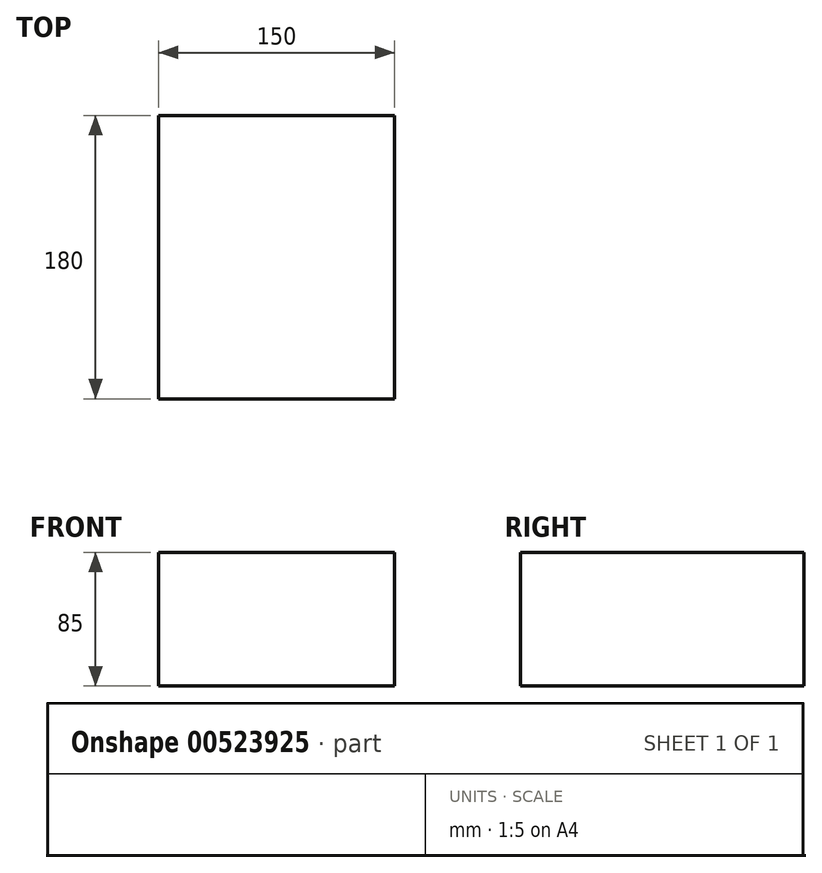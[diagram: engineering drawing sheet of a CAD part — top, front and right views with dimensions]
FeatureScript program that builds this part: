
annotation { "Feature Type Name" : "Feature", "Feature Type Description" : "" }
export const myFeature = defineFeature(function(context is Context, id is Id, definition is map)
    precondition{}
    {
        {
            var Q0;
            Q0=qCreatedBy(makeId("Front.planeOp"),FACE);
            var sketch = newSketch(context, id + "F0", { "sketchPlane" : qUnion([Q0])});
            skCircle(sketch, "E0", {"center": v(0, 0) * mm, "radius": 30 * mm});
            skSolve(sketch);
        }
        {
            var Q0;
            Q0=qSketchRegion(id+"F0",true);
            extrude(context, id + "F1", {"entities" : qUnion([Q0]), "depth" : 190 * mm});
        }
        {
            var Q0;
            Q0=makeQuery(id+"F1.opExtrude","CAP_FACE",FACE,{"disambiguationData":[OSD([sQuery(id+"F0.wireOp",EDGE,"E0")])],"isStart":true});
            var sketch = newSketch(context, id + "F2", { "sketchPlane" : qUnion([Q0])});
            skArc(sketch, "E1", {"start": v(0, 40) * mm, "mid": v(-40, 0) * mm, "end": v(0, -40) * mm});
            skLineSegment(sketch, "E2", {"start": v(0, 40) * mm, "end": v(50, 40) * mm});
            skLineSegment(sketch, "E3", {"start": v(50, 40) * mm, "end": v(50, -40) * mm});
            skLineSegment(sketch, "E4", {"start": v(50, -40) * mm, "end": v(0, -40) * mm});
            skSolve(sketch);
        }
        {
            var Q0;
            Q0=qSketchRegion(id+"F2",true);
            extrude(context, id + "F3", {"entities" : qUnion([Q0]), "operationType" : NewBodyOperationType.ADD, "oppositeDirection" : true, "depth" : 25 * mm});
        }
        {
            var Q0;
            Q0=makeQuery(id+"F3.opExtrude","CAP_FACE",FACE,{"disambiguationData":[OSD([sQuery(id+"F2.wireOp",EDGE,"E1"),sQuery(id+"F2.wireOp",EDGE,"E2"),sQuery(id+"F2.wireOp",EDGE,"E3"),sQuery(id+"F2.wireOp",EDGE,"E4")])],"isStart":false});
            var sketch = newSketch(context, id + "F4", { "sketchPlane" : qUnion([Q0])});
            skCircle(sketch, "E5", {"center": v(0, 0) * mm, "radius": 40 * mm});
            skSolve(sketch);
        }
        {
            var Q0;
            Q0=qSketchRegion(id+"F4",true);
            extrude(context, id + "F5", {"entities" : qUnion([Q0]), "operationType" : NewBodyOperationType.ADD, "depth" : 35 * mm});
        }
        {
            var Q0;
            Q0=qCreatedBy(makeId("Front.planeOp"),FACE);
            var sketch = newSketch(context, id + "F6", { "sketchPlane" : qUnion([Q0])});
            skLineSegment(sketch, "E6.bottom", {"start": v(0, 0) * mm, "end": v(170, 0) * mm});
            skLineSegment(sketch, "E6.top", {"start": v(0, 170) * mm, "end": v(170, 170) * mm});
            skLineSegment(sketch, "E6.left", {"start": v(0, 0) * mm, "end": v(0, 170) * mm});
            skLineSegment(sketch, "E6.right", {"start": v(170, 0) * mm, "end": v(170, 170) * mm});
            skCircle(sketch, "E7", {"center": v(6.35, 159.84) * mm, "radius": 2 * mm});
            skCircle(sketch, "E8", {"center": v(163.83, 136.98) * mm, "radius": 2 * mm});
            skCircle(sketch, "E9", {"center": v(163.83, 4.9) * mm, "radius": 2 * mm});
            skCircle(sketch, "E10", {"center": v(6.35, 4.9) * mm, "radius": 2 * mm});
            skSolve(sketch);
        }
        {
            var Q0;
            Q0=qSketchRegion(id+"F6",true);
            extrude(context, id + "F7", {"entities" : qUnion([Q0]), "depth" : 2 * mm});
        }
        {
            var Q0;
            Q0=makeQuery(id+"F7.opExtrude","SWEPT_BODY",BODY,{"disambiguationData":[OSD([sQuery(id+"F6.wireOp",EDGE,"E6.bottom"),sQuery(id+"F6.wireOp",EDGE,"E6.top"),sQuery(id+"F6.wireOp",EDGE,"E6.left"),sQuery(id+"F6.wireOp",EDGE,"E6.right"),sQuery(id+"F6.wireOp",EDGE,"E7"),sQuery(id+"F6.wireOp",EDGE,"E8"),sQuery(id+"F6.wireOp",EDGE,"E9"),sQuery(id+"F6.wireOp",EDGE,"E10")])]});
            deleteBodies(context, id + "F8", {"entities" : qUnion([Q0])});
        }
        {
            var Q0;
            Q0=qCreatedBy(makeId("Front.planeOp"),FACE);
            var sketch = newSketch(context, id + "F9", { "sketchPlane" : qUnion([Q0])});
            skLineSegment(sketch, "E11.bottom", {"start": v(0, 0) * mm, "end": v(150, 0) * mm});
            skLineSegment(sketch, "E11.top", {"start": v(0, 85) * mm, "end": v(150, 85) * mm});
            skLineSegment(sketch, "E11.left", {"start": v(0, 0) * mm, "end": v(0, 85) * mm});
            skLineSegment(sketch, "E11.right", {"start": v(150, 0) * mm, "end": v(150, 85) * mm});
            skSolve(sketch);
        }
        {
            var Q0;
            Q0=qSketchRegion(id+"F9",true);
            extrude(context, id + "F10", {"entities" : qUnion([Q0]), "depth" : 180 * mm});
        }
        {
            var Q0;
            Q0=makeQuery(id+"F1.opExtrude","SWEPT_BODY",BODY,{"disambiguationData":[OSD([sQuery(id+"F0.wireOp",EDGE,"E0")])]});
            deleteBodies(context, id + "F11", {"entities" : qUnion([Q0])});
        }
    });
